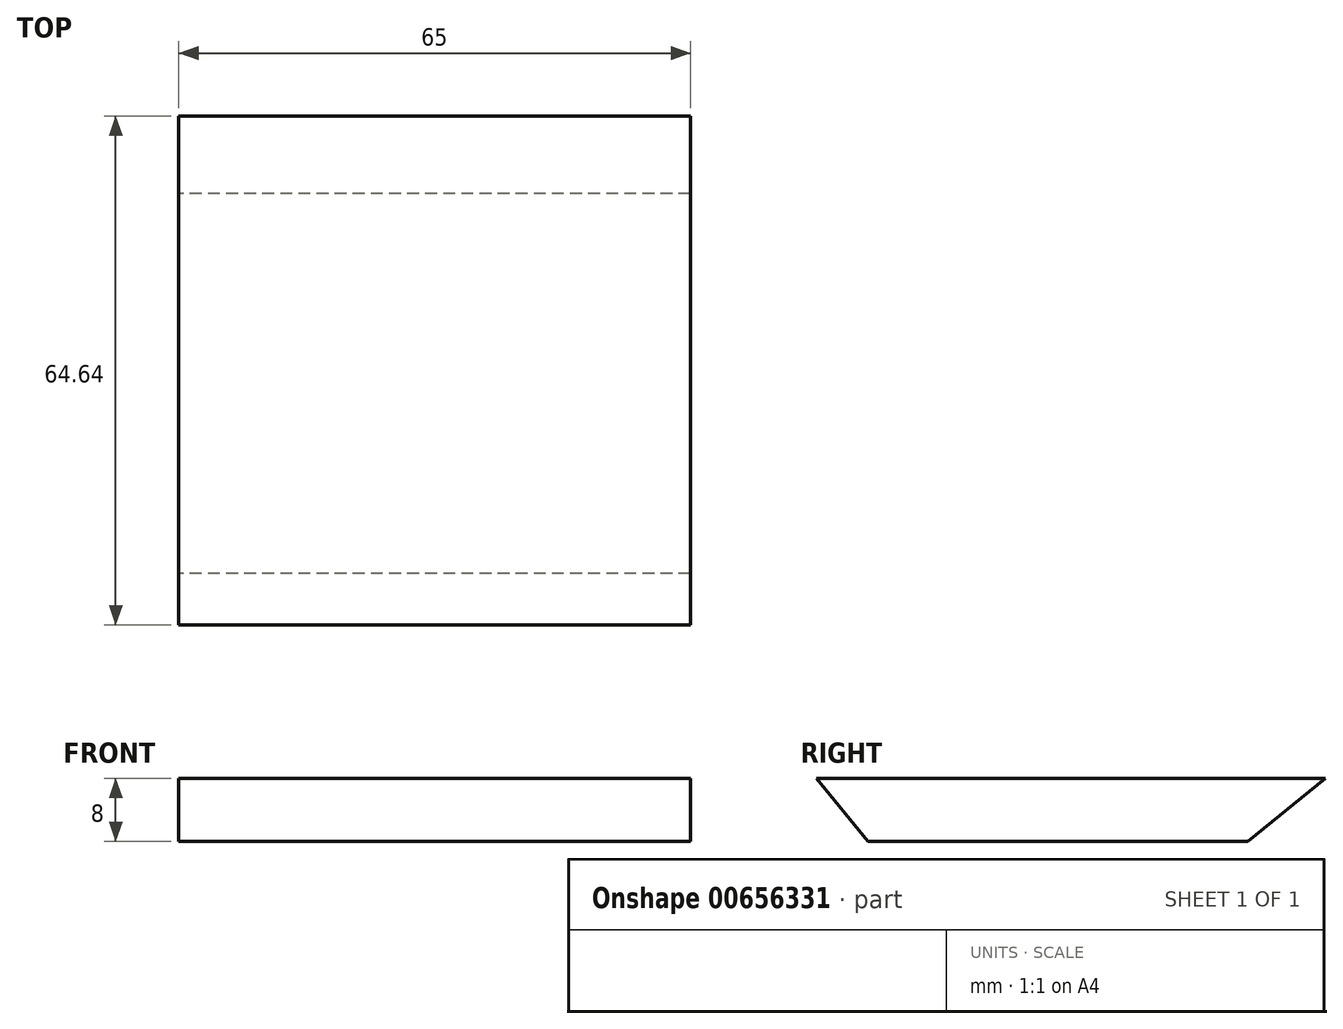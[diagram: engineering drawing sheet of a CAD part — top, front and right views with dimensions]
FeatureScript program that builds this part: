
annotation { "Feature Type Name" : "Feature", "Feature Type Description" : "" }
export const myFeature = defineFeature(function(context is Context, id is Id, definition is map)
    precondition{}
    {
        {
            var Q0;
            Q0=qCreatedBy(makeId("Top.planeOp"),FACE);
            var sketch = newSketch(context, id + "F0", { "sketchPlane" : qUnion([Q0])});
            skLineSegment(sketch, "E0.bottom", {"start": v(32.5, 24.15) * mm, "end": v(-32.5, 24.15) * mm});
            skLineSegment(sketch, "E0.top", {"start": v(32.5, -24.15) * mm, "end": v(-32.5, -24.15) * mm});
            skLineSegment(sketch, "E0.left", {"start": v(32.5, 24.15) * mm, "end": v(32.5, -24.15) * mm});
            skLineSegment(sketch, "E0.right", {"start": v(-32.5, 24.15) * mm, "end": v(-32.5, -24.15) * mm});
            skPoint(sketch, "E0.middle", {"position": v(0, 0) * mm});
            skSolve(sketch);
        }
        {
            var Q0;
            Q0=makeQuery(id+"F0.imprint","IMPRINT",FACE,{"disambiguationData":[TD([[makeQuery(id+"F0.imprint","IMPRINT",EDGE,{"derivedFrom":sQuery(id+"F0.wireOp",EDGE,"E0.bottom")}),1.0]])]});
            extrude(context, id + "F1", {"entities" : qUnion([Q0]), "depth" : 8 * mm, "offsetDistance" : 25 * mm});
        }
        {
            var Q0;
            Q0=makeQuery(id+"F1.opExtrude","SWEPT_FACE",FACE,{"disambiguationData":[OSD([sQuery(id+"F0.wireOp",EDGE,"E0.left")])]});
            var sketch = newSketch(context, id + "F2", { "sketchPlane" : qUnion([Q0])});
            skLineSegment(sketch, "E1", {"start": v(24.15, 8) * mm, "end": v(24.15, 0) * mm});
            skLineSegment(sketch, "E2", {"start": v(24.15, 0) * mm, "end": v(-4.9, -23.65) * mm});
            skLineSegment(sketch, "E3", {"start": v(-4.9, -23.65) * mm, "end": v(-24.15, 0) * mm});
            skLineSegment(sketch, "E4", {"start": v(24.15, 0) * mm, "end": v(33.98, 8) * mm});
            skLineSegment(sketch, "E5", {"start": v(33.98, 8) * mm, "end": v(24.15, 8) * mm});
            skLineSegment(sketch, "E6", {"start": v(-24.15, 0) * mm, "end": v(-30.66, 8) * mm});
            skLineSegment(sketch, "E7", {"start": v(-30.66, 8) * mm, "end": v(-24.15, 8) * mm});
            skLineSegment(sketch, "E8", {"start": v(-24.15, 8) * mm, "end": v(-24.15, 0) * mm});
            skSolve(sketch);
        }
        {
            var Q0;
            Q0=makeQuery(id+"F2.imprint","IMPRINT",FACE,{"disambiguationData":[TD([[makeQuery(id+"F2.imprint","IMPRINT",EDGE,{"derivedFrom":sQuery(id+"F2.wireOp",EDGE,"E1")}),1.0]])]});
            var Q1;
            Q1=makeQuery(id+"F2.imprint","IMPRINT",FACE,{"disambiguationData":[TD([[makeQuery(id+"F2.imprint","IMPRINT",EDGE,{"derivedFrom":sQuery(id+"F2.wireOp",EDGE,"E6")}),-1.0]])]});
            var Q2;
            Q2=makeQuery(id+"F1.opExtrude","SWEPT_FACE",FACE,{"disambiguationData":[OSD([sQuery(id+"F0.wireOp",EDGE,"E0.right")])]});
            extrude(context, id + "F3", {"entities" : qUnion([Q0, Q1]), "operationType" : NewBodyOperationType.ADD, "endBound" : BoundingType.UP_TO_SURFACE, "oppositeDirection" : true, "depth" : 25 * mm, "endBoundEntityFace" : qUnion([Q2]), "offsetDistance" : 25 * mm});
        }
    });
